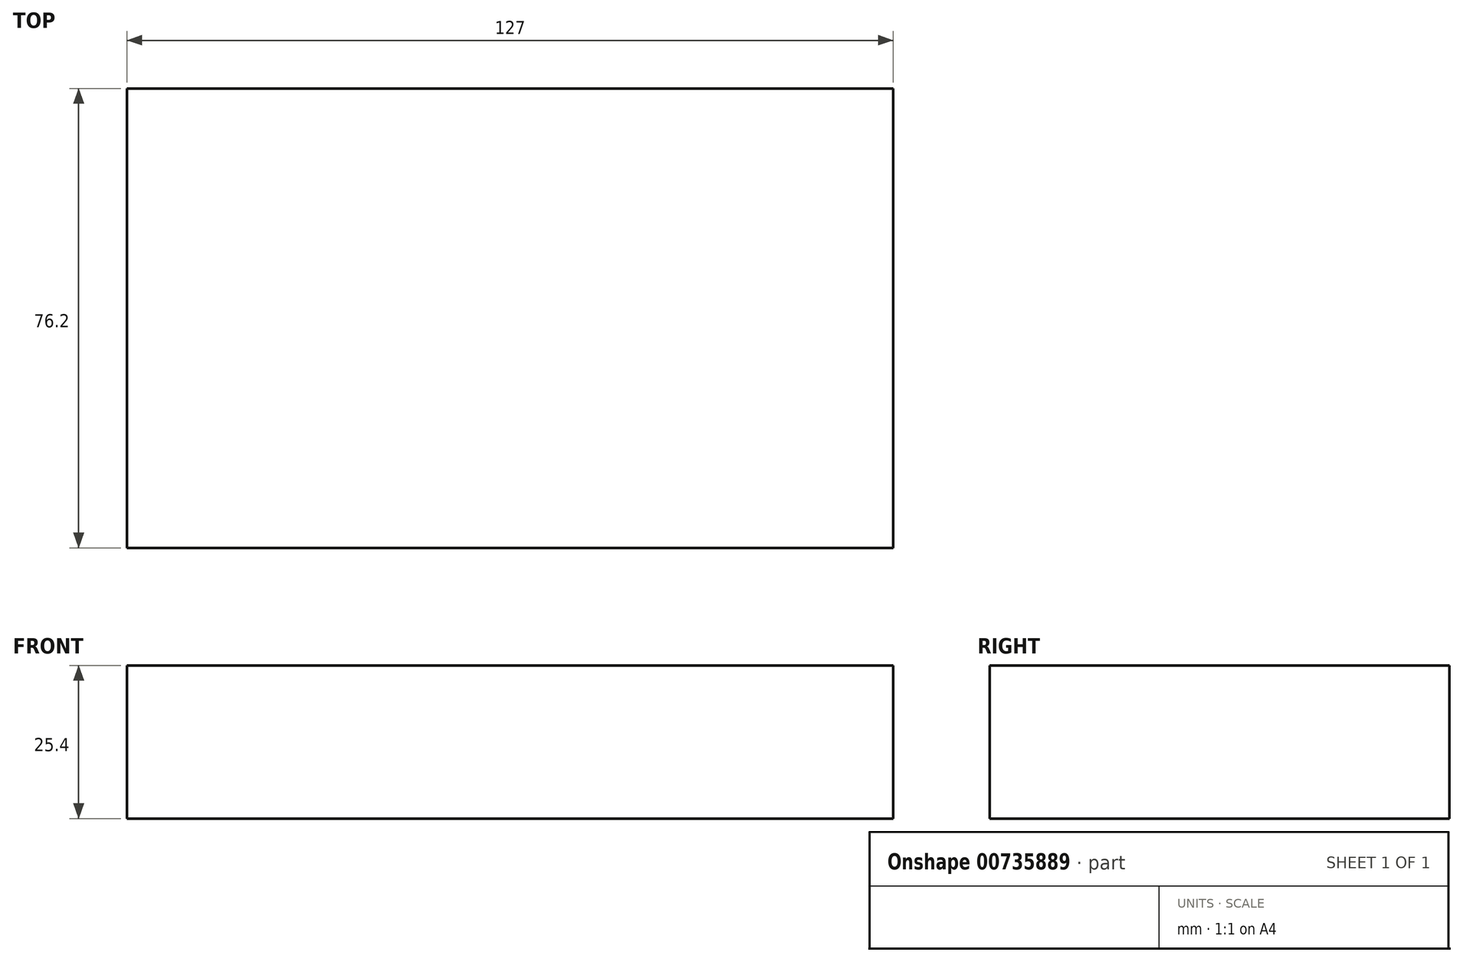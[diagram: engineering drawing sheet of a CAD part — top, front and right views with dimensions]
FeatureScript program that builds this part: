
annotation { "Feature Type Name" : "Feature", "Feature Type Description" : "" }
export const myFeature = defineFeature(function(context is Context, id is Id, definition is map)
    precondition{}
    {
        {
            var Q0;
            Q0=qCreatedBy(makeId("Top.planeOp"),FACE);
            var sketch = newSketch(context, id + "F0", { "sketchPlane" : qUnion([Q0])});
            skLineSegment(sketch, "E0.bottom", {"start": v(0, 0) * mm, "end": v(127, 0) * mm});
            skLineSegment(sketch, "E0.top", {"start": v(0, -76.2) * mm, "end": v(127, -76.2) * mm});
            skLineSegment(sketch, "E0.left", {"start": v(0, 0) * mm, "end": v(0, -76.2) * mm});
            skLineSegment(sketch, "E0.right", {"start": v(127, 0) * mm, "end": v(127, -76.2) * mm});
            skSolve(sketch);
        }
        {
            var Q0;
            Q0=makeQuery(id+"F0.imprint","IMPRINT",FACE,{"disambiguationData":[TD([[makeQuery(id+"F0.imprint","IMPRINT",EDGE,{"derivedFrom":sQuery(id+"F0.wireOp",EDGE,"E0.bottom")}),-1.0]])]});
            extrude(context, id + "F1", {"entities" : qUnion([Q0]), "depth" : 25.4 * mm, "offsetDistance" : 25.4 * mm});
        }
    });
